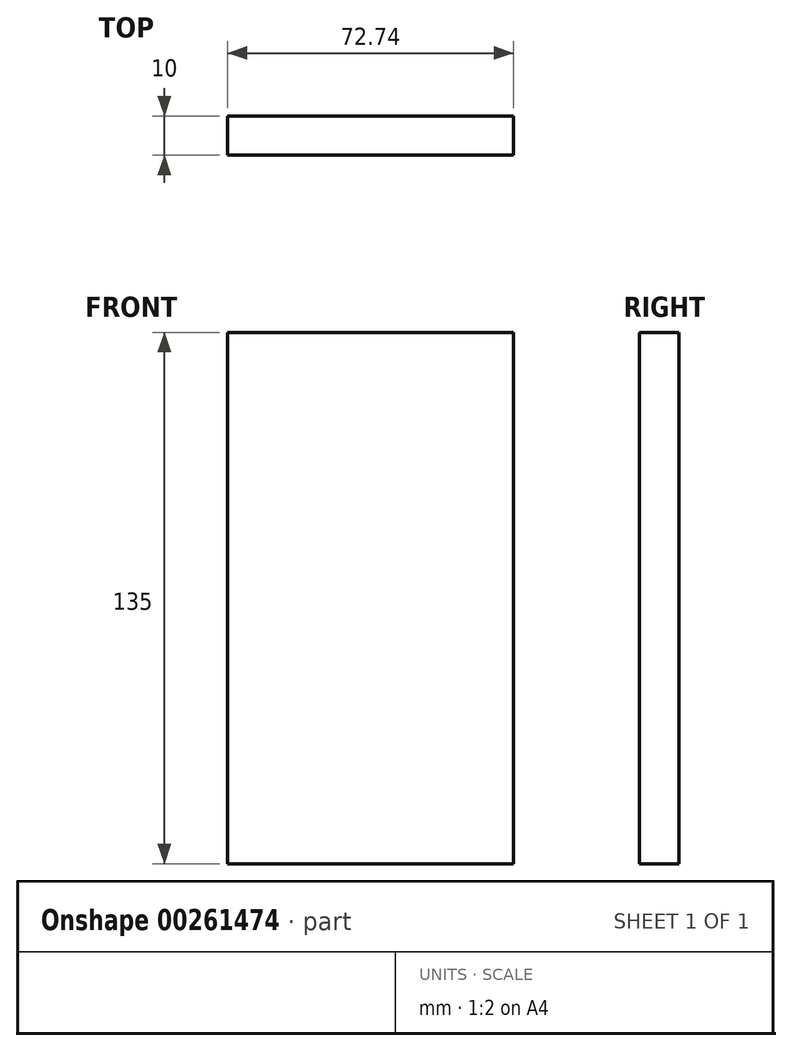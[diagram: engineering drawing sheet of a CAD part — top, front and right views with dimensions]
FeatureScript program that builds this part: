
annotation { "Feature Type Name" : "Feature", "Feature Type Description" : "" }
export const myFeature = defineFeature(function(context is Context, id is Id, definition is map)
    precondition{}
    {
        {
            var Q0;
            Q0=qCreatedBy(makeId("Front.planeOp"),FACE);
            var sketch = newSketch(context, id + "F0", { "sketchPlane" : qUnion([Q0])});
            skLineSegment(sketch, "E0.bottom", {"start": v(-36.37, 67.5) * mm, "end": v(36.37, 67.5) * mm});
            skLineSegment(sketch, "E0.top", {"start": v(-36.37, -67.5) * mm, "end": v(36.37, -67.5) * mm});
            skLineSegment(sketch, "E0.left", {"start": v(-36.37, 67.5) * mm, "end": v(-36.37, -67.5) * mm});
            skLineSegment(sketch, "E0.right", {"start": v(36.37, 67.5) * mm, "end": v(36.37, -67.5) * mm});
            skPoint(sketch, "E0.middle", {"position": v(0, 0) * mm});
            skSolve(sketch);
        }
        {
            var Q0;
            Q0=makeQuery(id+"F0.imprint","IMPRINT",FACE,{"disambiguationData":[TD([[makeQuery(id+"F0.imprint","IMPRINT",EDGE,{"derivedFrom":sQuery(id+"F0.wireOp",EDGE,"E0.bottom")}),-1.0]])]});
            extrude(context, id + "F1", {"entities" : qUnion([Q0]), "depth" : 10 * mm});
        }
        {
            var Q0;
            Q0=makeQuery(id+"F1.opExtrude","SWEPT_EDGE",EDGE,{"disambiguationData":[OSD([sQuery(id+"F0.wireOp",EDGE,"E0.bottom"),sQuery(id+"F0.wireOp",EDGE,"E0.right")])]});
            var Q1;
            Q1=makeQuery(id+"F1.opExtrude","SWEPT_EDGE",EDGE,{"disambiguationData":[OSD([sQuery(id+"F0.wireOp",EDGE,"E0.bottom"),sQuery(id+"F0.wireOp",EDGE,"E0.left")])]});
            var Q2;
            Q2=makeQuery(id+"F1.opExtrude","SWEPT_EDGE",EDGE,{"disambiguationData":[OSD([sQuery(id+"F0.wireOp",EDGE,"E0.top"),sQuery(id+"F0.wireOp",EDGE,"E0.left")])]});
            var Q3;
            Q3=makeQuery(id+"F1.opExtrude","SWEPT_EDGE",EDGE,{"disambiguationData":[OSD([sQuery(id+"F0.wireOp",EDGE,"E0.top"),sQuery(id+"F0.wireOp",EDGE,"E0.right")])]});
            fillet(context, id + "F2", {"entities" : qUnion([Q0, Q1, Q2, Q3]), "radius" : 10 * mm, "tangentPropagation" : true, "allowEdgeOverflow" : false});
        }
        {
            var Q0;
            Q0=qCreatedBy(makeId("Front.planeOp"),FACE);
            var sketch = newSketch(context, id + "F3", { "sketchPlane" : qUnion([Q0])});
            skLineSegment(sketch, "E1.bottom", {"start": v(33.5, 66.5) * mm, "end": v(-33.5, 66.5) * mm});
            skLineSegment(sketch, "E1.top", {"start": v(33.5, -66.5) * mm, "end": v(-33.5, -66.5) * mm});
            skLineSegment(sketch, "E1.left", {"start": v(33.5, 66.5) * mm, "end": v(33.5, -66.5) * mm});
            skLineSegment(sketch, "E1.right", {"start": v(-33.5, 66.5) * mm, "end": v(-33.5, -66.5) * mm});
            skPoint(sketch, "E1.middle", {"position": v(0, 0) * mm});
            skSolve(sketch);
        }
        {
            var Q0;
            Q0=makeQuery(id+"F3.imprint","IMPRINT",FACE,{"disambiguationData":[TD([[makeQuery(id+"F3.imprint","IMPRINT",EDGE,{"derivedFrom":sQuery(id+"F3.wireOp",EDGE,"E1.bottom")}),1.0]])]});
            extrude(context, id + "F4", {"entities" : qUnion([Q0]), "operationType" : NewBodyOperationType.REMOVE, "depth" : 8 * mm});
        }
        {
            var Q0;
            Q0=makeQuery(id+"F1.opExtrude","SWEPT_FACE",FACE,{"disambiguationData":[OSD([sQuery(id+"F0.wireOp",EDGE,"E0.top")])]});
            var sketch = newSketch(context, id + "F5", { "sketchPlane" : qUnion([Q0])});
            skLineSegment(sketch, "E2.bottom", {"start": v(-12.95, 3.48) * mm, "end": v(-24.97, 3.48) * mm});
            skLineSegment(sketch, "E2.top", {"start": v(-12.95, 6.52) * mm, "end": v(-24.97, 6.52) * mm});
            skLineSegment(sketch, "E2.left", {"start": v(-12.95, 3.48) * mm, "end": v(-12.95, 6.52) * mm});
            skLineSegment(sketch, "E2.right", {"start": v(-24.97, 3.48) * mm, "end": v(-24.97, 6.52) * mm});
            skSolve(sketch);
        }
        {
            var Q0;
            Q0 = qSketchRegion(id + "F5", true);
            extrude(context, id + "F6", {"entities" : qUnion([Q0]), "operationType" : NewBodyOperationType.REMOVE, "oppositeDirection" : true, "depth" : 25 * mm});
        }
        {
            var Q0;
            Q0=makeQuery(id+"F1.opExtrude","SWEPT_FACE",FACE,{"disambiguationData":[OSD([sQuery(id+"F0.wireOp",EDGE,"E0.bottom")])]});
            var sketch = newSketch(context, id + "F7", { "sketchPlane" : qUnion([Q0])});
            skCircle(sketch, "E3", {"center": v(-14.32, -4.63) * mm, "radius": 3.17 * mm});
            skSolve(sketch);
        }
        {
            var Q0;
            Q0 = qSketchRegion(id + "F7", true);
            extrude(context, id + "F8", {"entities" : qUnion([Q0]), "operationType" : NewBodyOperationType.REMOVE, "oppositeDirection" : true, "depth" : 12 * mm});
        }
        {
            var Q0;
            Q0=makeQuery(id+"F1.opExtrude","SWEPT_FACE",FACE,{"disambiguationData":[OSD([sQuery(id+"F0.wireOp",EDGE,"E0.left")])]});
            var sketch = newSketch(context, id + "F9", { "sketchPlane" : qUnion([Q0])});
            skLineSegment(sketch, "E4.bottom", {"start": v(2.68, 0) * mm, "end": v(5.52, 0) * mm});
            skLineSegment(sketch, "E4.top", {"start": v(2.68, 53.28) * mm, "end": v(5.52, 53.28) * mm});
            skLineSegment(sketch, "E4.left", {"start": v(2.68, 0) * mm, "end": v(2.68, 53.28) * mm});
            skLineSegment(sketch, "E4.right", {"start": v(5.52, 0) * mm, "end": v(5.52, 53.28) * mm});
            skSolve(sketch);
        }
        {
            var Q0;
            Q0 = qSketchRegion(id + "F9", true);
            extrude(context, id + "F10", {"entities" : qUnion([Q0]), "operationType" : NewBodyOperationType.REMOVE, "oppositeDirection" : true, "depth" : 12 * mm});
        }
        {
            var Q0;
            Q0=makeQuery(id+"F3.imprint","IMPRINT",FACE,{"disambiguationData":[TD([[makeQuery(id+"F3.imprint","IMPRINT",EDGE,{"derivedFrom":sQuery(id+"F3.wireOp",EDGE,"E1.bottom")}),1.0]])]});
            extrude(context, id + "F11", {"entities" : qUnion([Q0]), "depth" : 8 * mm});
        }
        {
            var Q0;
            Q0 = qSketchRegion(id + "F3", true);
            extrude(context, id + "F12", {"entities" : qUnion([Q0]), "operationType" : NewBodyOperationType.REMOVE, "depth" : 8 * mm});
        }
        {
            var Q0;
            Q0=makeQuery(id+"F0.imprint","IMPRINT",FACE,{"disambiguationData":[TD([[makeQuery(id+"F0.imprint","IMPRINT",EDGE,{"derivedFrom":sQuery(id+"F0.wireOp",EDGE,"E0.bottom")}),-1.0]])]});
            extrude(context, id + "F13", {"entities" : qUnion([Q0]), "operationType" : NewBodyOperationType.ADD, "depth" : 10 * mm});
        }
    });
